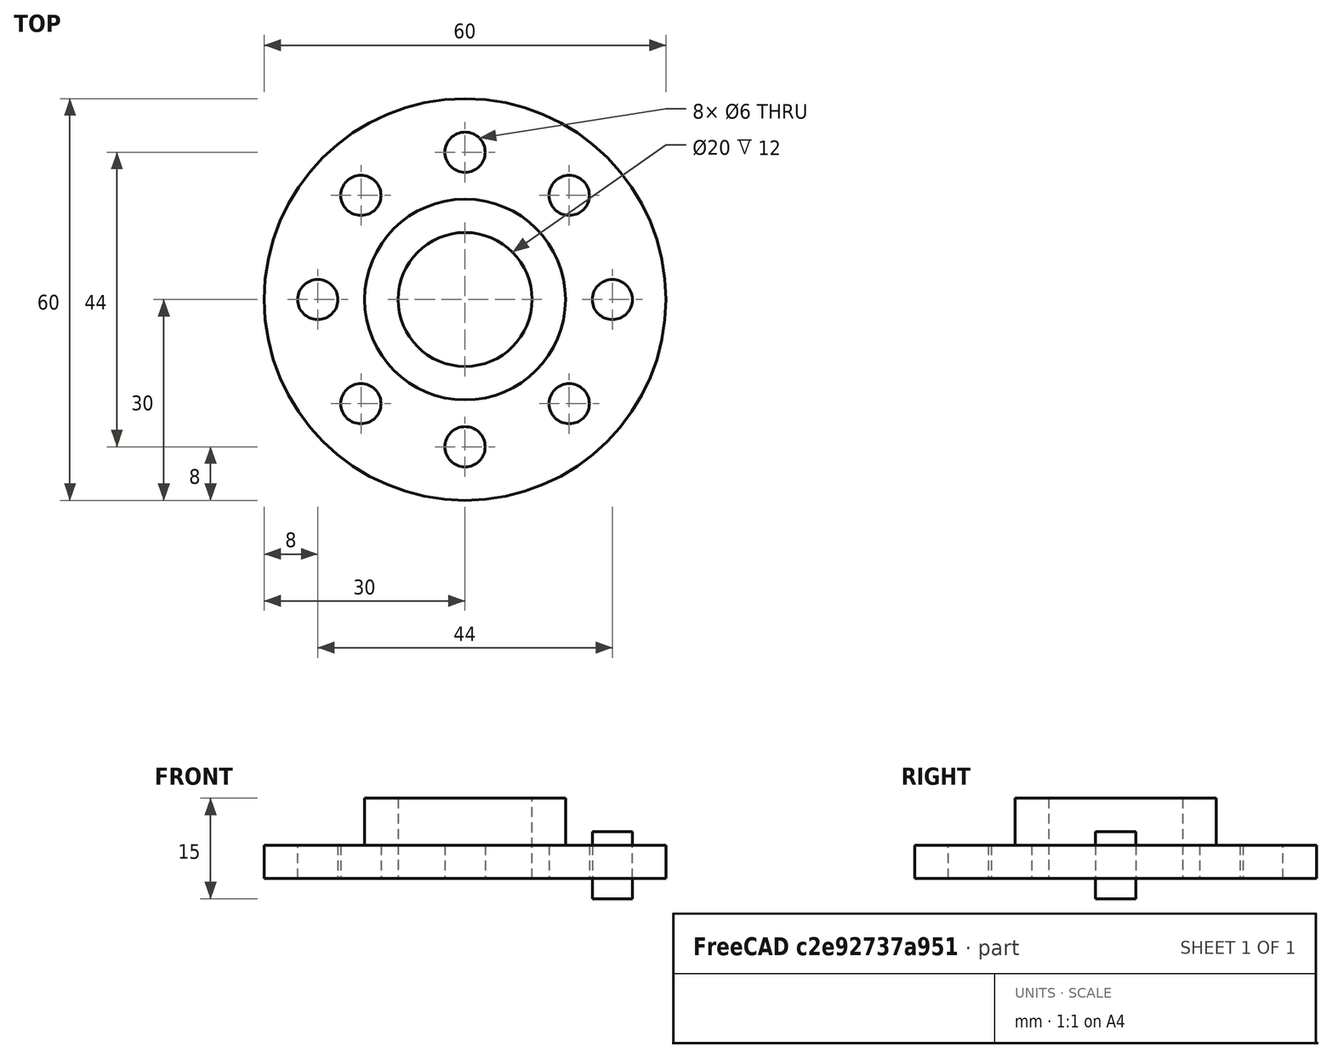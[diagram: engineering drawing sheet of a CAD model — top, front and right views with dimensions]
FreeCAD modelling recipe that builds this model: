
FCSTD DOCUMENT  (FreeCAD 0.21R33694 (Git))
Label: OJT1_T11P01.terror
License: All rights reserved
LicenseURL: http://en.wikipedia.org/wiki/All_rights_reserved
objects: Part::Cylinder×4, Part::Cut×2, Part::Fuse×1, Part::FeaturePython×1
note: 7 computed .brp shape members not serialized (recipe doc carries the construction recipe); baked Part::Feature solids carry a one-line shape summary decoded from their .brp

FEATURE [Part::Cylinder] Cylinder  label="Cilindre"
  Angle = 360
  AttacherType = Attacher::AttachEngine3D
  FirstAngle = 0
  Height = 5
  Radius = 30
  SecondAngle = 0
FEATURE [Part::Cylinder] Cylinder001  label="Cilindre001"
  Angle = 360
  AttacherType = Attacher::AttachEngine3D
  FirstAngle = 0
  Height = 12
  Radius = 15
  SecondAngle = 0
FEATURE [Part::Cylinder] Cylinder002  label="Cilindre002"
  Angle = 360
  AttacherType = Attacher::AttachEngine3D
  FirstAngle = 0
  Height = 30
  Placement = pos=(0,0,-9) rot=(0,0,1;0rad)
  Radius = 10
  SecondAngle = 0
FEATURE [Part::Fuse] Fusion
  Base = -> Cylinder
  Refine = true
  Tool = -> Cylinder001
FEATURE [Part::Cut] Cut
  Base = -> Fusion
  Refine = true
  Tool = -> Cylinder002
FEATURE [Part::Cylinder] Cylinder003  label="Cilindre003"
  Angle = 360
  AttacherType = Attacher::AttachEngine3D
  FirstAngle = 0
  Height = 10
  Placement = pos=(22,0,-3) rot=(0,0,1;0rad)
  Radius = 3
  SecondAngle = 0
FEATURE [Part::FeaturePython] Array  # Draft array (typed FeaturePython)
  AlwaysSyncPlacement = false
  Angle = 360
  ArrayType = 1
  Axis = (0,0,1)
  Base = -> Cylinder003
  Center = (0,0,0)
  Count = 8
  ExpandArray = false
  Fuse = false
  IntervalAxis = (0,0,0)
  IntervalX = (50,0,0)
  IntervalY = (0,50,0)
  IntervalZ = (0,0,50)
  NumberCircles = 3
  NumberPolar = 8
  NumberX = 2
  NumberY = 2
  NumberZ = 1
  PlacementList = 8 placements: [(22,0,-3),(15.5563,15.5563,-3),(0,22,-3),(-15.5563,15.5563,-3),(-22,2.69422e-15,-3),(-15.5563,-15.5563,-3),(-4.88498e-15,-22,-3),(15.5563,-15.5563,-3)]
  RadialDistance = 50
  ScaleList = (8) [(1,1,1),(1,1,1),(1,1,1),(1,1,1),(1,1,1),(1,1,1),(1,1,1),(1,1,1)]
  Symmetry = 1
  TangentialDistance = 25
FEATURE [Part::Cut] Cut001
  Base = -> Cut
  Refine = true
  Tool = -> Array
